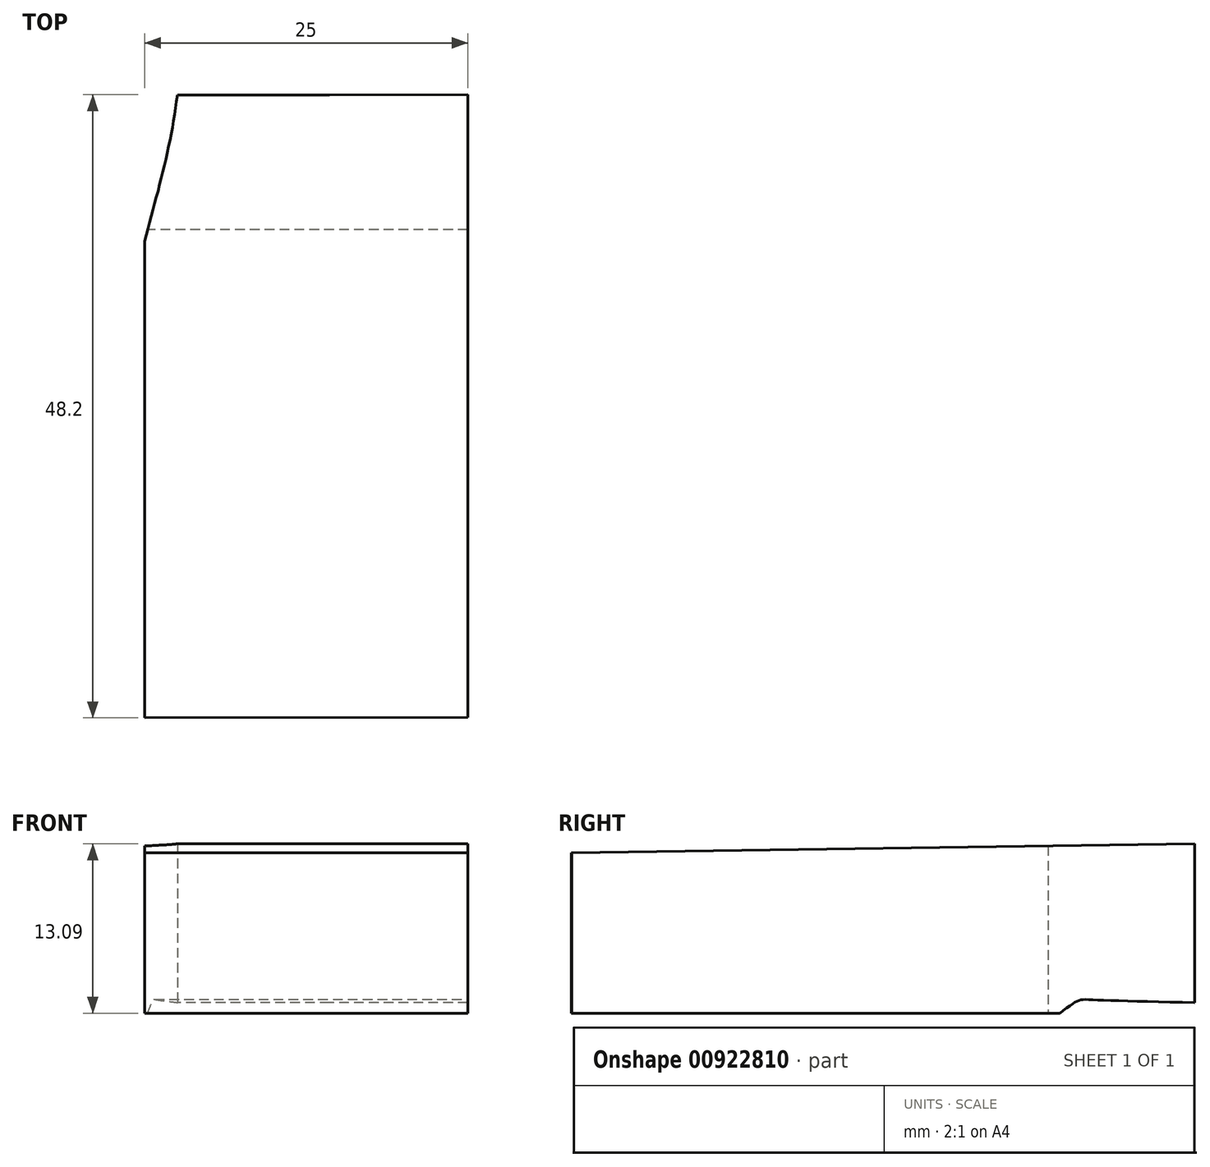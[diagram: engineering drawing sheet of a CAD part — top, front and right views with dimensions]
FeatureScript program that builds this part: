
annotation { "Feature Type Name" : "Feature", "Feature Type Description" : "" }
export const myFeature = defineFeature(function(context is Context, id is Id, definition is map)
    precondition{}
    {
        {
            var Q0;
            Q0=qCreatedBy(makeId("Top.planeOp"),FACE);
            var sketch = newSketch(context, id + "F0", { "sketchPlane" : qUnion([Q0])});
            skArc(sketch, "E0", {"start": v(22.14, 65.18) * mm, "mid": v(-1.93, 67.66) * mm, "end": v(-26, 65.1) * mm, "construction": true});
            skFitSpline(sketch, "E1", {"points": [v(-26, 65.1) * mm, v(-30.36, 2.08) * mm, v(-29.82, -44.68) * mm, v(-28.25, -67.77) * mm, v(-26, -73.31) * mm, v(-18.2, -76.06) * mm, v(-2.03, -76.93) * mm], "startDerivative": vector(-24.36, -220.35) * mm, "endDerivative": vector(126.06, -1.63) * mm});
            skFitSpline(sketch, "E2", {"points": [v(-27.23, -3.45) * mm, v(-27.13, 2.02) * mm, v(-24.6, 9.02) * mm, v(-20.54, 18.65) * mm, v(-17.8, 28.58) * mm, v(-14.76, 40.14) * mm, v(-13.95, 44.73) * mm], "startDerivative": vector(-2.53, 39.57) * mm, "endDerivative": vector(4.94, 32.68) * mm});
            skLineSegment(sketch, "E3", {"start": v(-13.95, 44.73) * mm, "end": v(-2.18, 44.73) * mm});
            skCircle(sketch, "E4", {"center": v(-20.6, 45.26) * mm, "radius": 2.34 * mm});
            skLineSegment(sketch, "E5", {"start": v(-2.03, -76.93) * mm, "end": v(-2.18, 44.73) * mm, "construction": true});
            skFitSpline(sketch, "E6.MirrorCS", {"points": [v(21.57, 65.17) * mm, v(26.1, 2.16) * mm, v(25.68, -44.61) * mm, v(24.17, -67.7) * mm, v(21.92, -73.25) * mm, v(14.13, -76.02) * mm, v(-2.03, -76.93) * mm], "startDerivative": vector(24.91, -220.29) * mm, "endDerivative": vector(-126.06, -1.94) * mm});
            skFitSpline(sketch, "E7.MirrorCS", {"points": [v(22.98, -3.39) * mm, v(22.86, 2.09) * mm, v(20.31, 9.07) * mm, v(16.23, 18.7) * mm, v(13.47, 28.62) * mm, v(10.4, 40.17) * mm, v(9.58, 44.76) * mm], "startDerivative": vector(2.43, 39.58) * mm, "endDerivative": vector(-5.02, 32.67) * mm});
            skLineSegment(sketch, "E8.MirrorCS", {"start": v(9.58, 44.76) * mm, "end": v(-2.18, 44.73) * mm});
            skLineSegment(sketch, "E9", {"start": v(22.98, -3.39) * mm, "end": v(-27.23, -3.45) * mm});
            skSolve(sketch);
        }
        {
            var Q0;
            Q0=qCreatedBy(makeId("Right.planeOp"),FACE);
            var sketch = newSketch(context, id + "F1", { "sketchPlane" : qUnion([Q0])});
            skFitSpline(sketch, "E10", {"points": [v(-7.68, -12.1) * mm, v(-6.26, -17.38) * mm, v(-1.2, -30.35) * mm, v(2.76, -49.71) * mm, v(3.27, -54.48) * mm, v(5.5, -57.92) * mm, v(5.7, -59.54) * mm, v(5.4, -83.47) * mm, v(5.7, -84.68) * mm, v(7.32, -86.5) * mm, v(12.6, -87.22) * mm, v(18.07, -87.52) * mm], "startDerivative": vector(12.54, -58.92) * mm, "endDerivative": vector(63.87, -4.9) * mm});
            skLineSegment(sketch, "E11", {"start": v(-7.68, -12.1) * mm, "end": v(16.97, -12.1) * mm});
            skLineSegment(sketch, "E12", {"start": v(16.97, -12.1) * mm, "end": v(18.07, -87.52) * mm});
            skSolve(sketch);
        }
        {
            var Q0;
            Q0=makeQuery(id+"F0.imprint","IMPRINT",FACE,{"disambiguationData":[TD([[makeQuery(id+"F0.imprint","IMPRINT",EDGE,{"derivedFrom":sQuery(id+"F0.wireOp",EDGE,"E2")}),-1.0]])]});
            extrude(context, id + "F2", {"entities" : qUnion([Q0]), "depth" : 25 * mm, "offsetDistance" : 25 * mm});
        }
        {
            var Q0;
            Q0=makeQuery(id+"F1.imprint","IMPRINT",FACE,{"disambiguationData":[TD([[makeQuery(id+"F1.imprint","IMPRINT",EDGE,{"derivedFrom":sQuery(id+"F1.wireOp",EDGE,"E10")}),1.0]])]});
            extrude(context, id + "F3", {"entities" : qUnion([Q0]), "depth" : 25 * mm, "offsetDistance" : 25 * mm});
        }
        {
            var Q0;
            Q0=makeQuery(id+"F3.opExtrude","SWEPT_BODY",BODY,{"disambiguationData":[OSD([sQuery(id+"F1.wireOp",EDGE,"E10"),sQuery(id+"F1.wireOp",EDGE,"E11"),sQuery(id+"F1.wireOp",EDGE,"E12")])]});
            var Q1;
            Q1=makeQuery(id+"F3.opExtrude","SWEPT_EDGE",EDGE,{"disambiguationData":[OSD([sQuery(id+"F1.wireOp",EDGE,"E11"),sQuery(id+"F1.wireOp",EDGE,"E12")])]});
            transform(context, id + "F4", {"entities" : qUnion([Q0]), "transformType" : TransformType.ROTATION, "transformAxis" : qUnion([Q1]), "angle" : 90 * degree, "oppositeDirection" : true, "makeCopy" : false});
        }
        {
            var Q0;
            Q0=makeQuery(id+"F2.opExtrude","SWEPT_BODY",BODY,{"disambiguationData":[OSD([sQuery(id+"F0.wireOp",EDGE,"E2"),sQuery(id+"F0.wireOp",EDGE,"E3"),sQuery(id+"F0.wireOp",EDGE,"E7.MirrorCS"),sQuery(id+"F0.wireOp",EDGE,"E8.MirrorCS"),sQuery(id+"F0.wireOp",EDGE,"E9")])]});
            transform(context, id + "F5", {"entities" : qUnion([Q0]), "transformType" : TransformType.TRANSLATION_3D, "dx" : 16.5 * mm, "dy" : 27.3 * mm, "dz" : -24.4 * mm, "makeCopy" : false});
        }
        {
            var Q0;
            Q0=makeQuery(id+"F2.opExtrude","SWEPT_BODY",BODY,{"disambiguationData":[OSD([sQuery(id+"F0.wireOp",EDGE,"E2"),sQuery(id+"F0.wireOp",EDGE,"E3"),sQuery(id+"F0.wireOp",EDGE,"E7.MirrorCS"),sQuery(id+"F0.wireOp",EDGE,"E8.MirrorCS"),sQuery(id+"F0.wireOp",EDGE,"E9")])]});
            var Q1;
            Q1=makeQuery(id+"F3.opExtrude","SWEPT_BODY",BODY,{"disambiguationData":[OSD([sQuery(id+"F1.wireOp",EDGE,"E10"),sQuery(id+"F1.wireOp",EDGE,"E11"),sQuery(id+"F1.wireOp",EDGE,"E12")])]});
            booleanBodies(context, id + "F6", {"operationType" : BooleanOperationType.INTERSECTION, "tools" : qUnion([Q0, Q1])});
        }
    });
